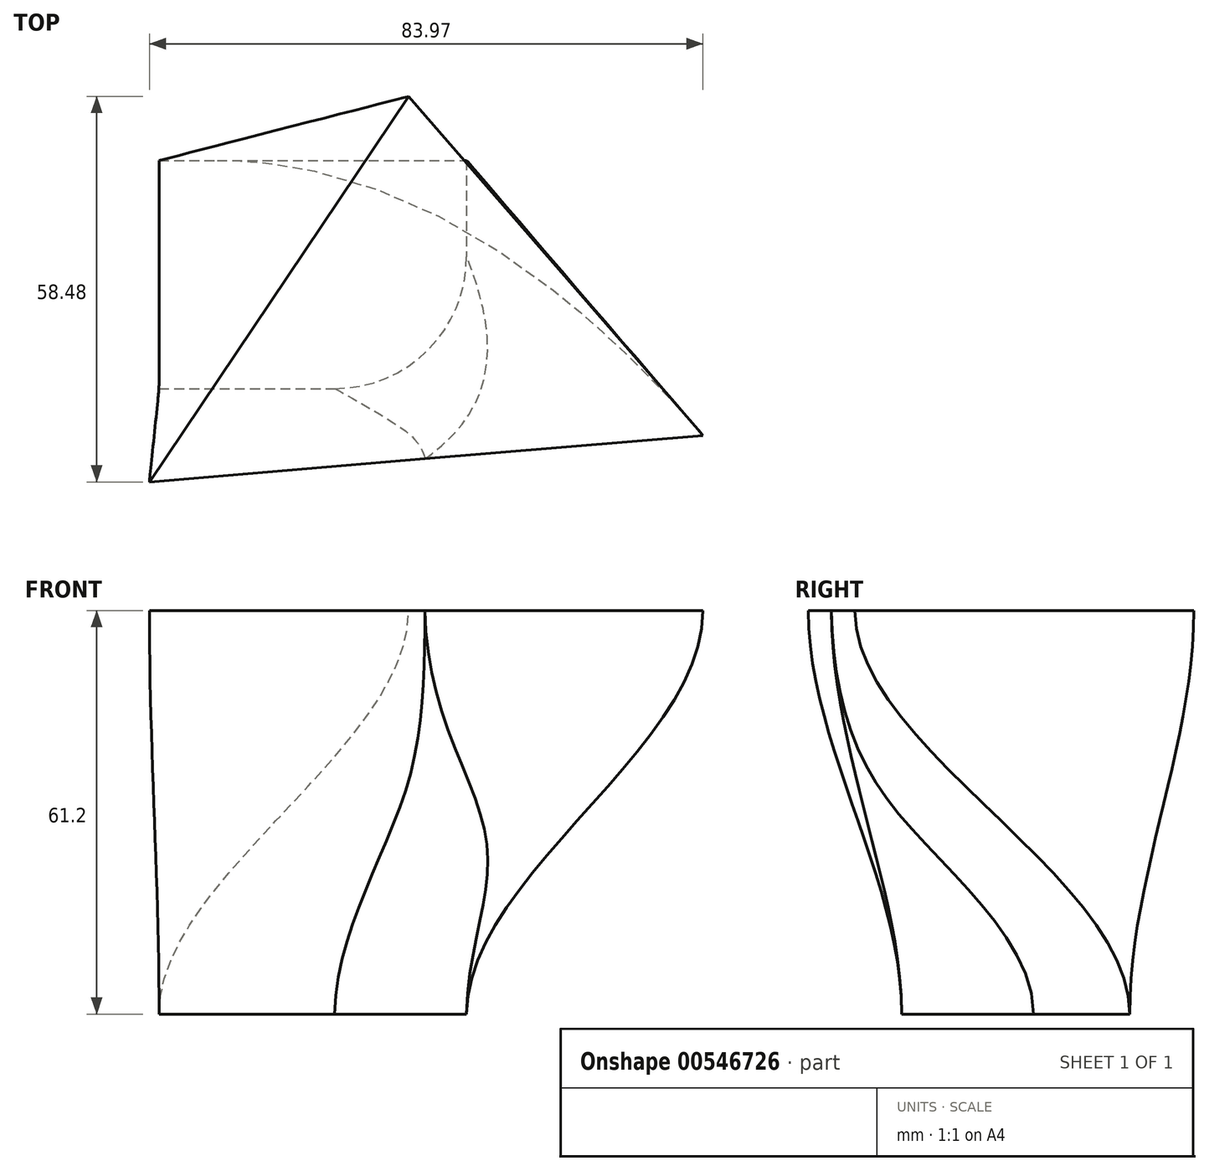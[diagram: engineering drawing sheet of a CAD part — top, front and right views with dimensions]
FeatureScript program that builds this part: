
annotation { "Feature Type Name" : "Feature", "Feature Type Description" : "" }
export const myFeature = defineFeature(function(context is Context, id is Id, definition is map)
    precondition{}
    {
        {
            var Q0;
            Q0=qCreatedBy(makeId("Top.planeOp"),FACE);
            var sketch = newSketch(context, id + "F0", { "sketchPlane" : qUnion([Q0])});
            skLineSegment(sketch, "E0.bottom", {"start": v(-20.33, 15.5) * mm, "end": v(26.33, 15.5) * mm});
            skLineSegment(sketch, "E0.top", {"start": v(-20.33, -19.1) * mm, "end": v(26.33, -19.1) * mm});
            skLineSegment(sketch, "E0.left", {"start": v(-20.33, 15.5) * mm, "end": v(-20.33, -19.1) * mm});
            skLineSegment(sketch, "E0.right", {"start": v(26.33, 15.5) * mm, "end": v(26.33, -19.1) * mm});
            skSolve(sketch);
        }
        {
            var Q0;
            Q0=qCreatedBy(makeId("Top.planeOp"),FACE);
            cPlane(context, id + "F1", {"entities" : qUnion([Q0]), "cplaneType" : CPlaneType.OFFSET, "offset" : 61.2 * mm, "width" : 150 * mm, "height" : 150 * mm});
        }
        {
            var Q0;
            Q0=qCreatedBy(id+"F1.planeOp",FACE);
            var sketch = newSketch(context, id + "F2", { "sketchPlane" : qUnion([Q0])});
            skLineSegment(sketch, "E1", {"start": v(-21.8, -33.27) * mm, "end": v(17.54, 25.2) * mm});
            skLineSegment(sketch, "E2", {"start": v(17.54, 25.2) * mm, "end": v(62.17, -26.2) * mm});
            skLineSegment(sketch, "E3", {"start": v(62.17, -26.2) * mm, "end": v(20.03, -29.75) * mm});
            skLineSegment(sketch, "E4", {"start": v(20.03, -29.75) * mm, "end": v(-21.8, -33.27) * mm});
            skSolve(sketch);
        }
        {
            var Q0;
            Q0=makeQuery(id+"F0.imprint","IMPRINT",FACE,{"disambiguationData":[TD([[makeQuery(id+"F0.imprint","IMPRINT",EDGE,{"derivedFrom":sQuery(id+"F0.wireOp",EDGE,"E0.bottom")}),-1.0]])]});
            var Q1;
            Q1=makeQuery(id+"F2.imprint","IMPRINT",FACE,{"disambiguationData":[TD([[makeQuery(id+"F2.imprint","IMPRINT",EDGE,{"derivedFrom":sQuery(id+"F2.wireOp",EDGE,"E1")}),-1.0]])]});
            loft(context, id + "F3", {"startCondition" : LoftEndDerivativeType.NORMAL_TO_PROFILE, "startMagnitude" : 1, "endCondition" : LoftEndDerivativeType.NORMAL_TO_PROFILE, "endMagnitude" : 1, "sheetProfilesArray" : [{ "sheetProfileEntities" : qUnion([Q0]) }, { "sheetProfileEntities" : qUnion([Q1]) }]});
        }
        {
            var Q0;
            Q0=makeQuery(id+"F3.opLoft","SWEPT_EDGE",EDGE,{"disambiguationData":[OSD([sQuery(id+"F0.wireOp",EDGE,"E0.top"),sQuery(id+"F0.wireOp",EDGE,"E0.right"),sQuery(id+"F2.wireOp",EDGE,"E3"),sQuery(id+"F2.wireOp",EDGE,"E4")])]});
            fillet(context, id + "F4", {"entities" : qUnion([Q0]), "radius" : 20 * mm, "tangentPropagation" : true, "allowEdgeOverflow" : false});
        }
    });
